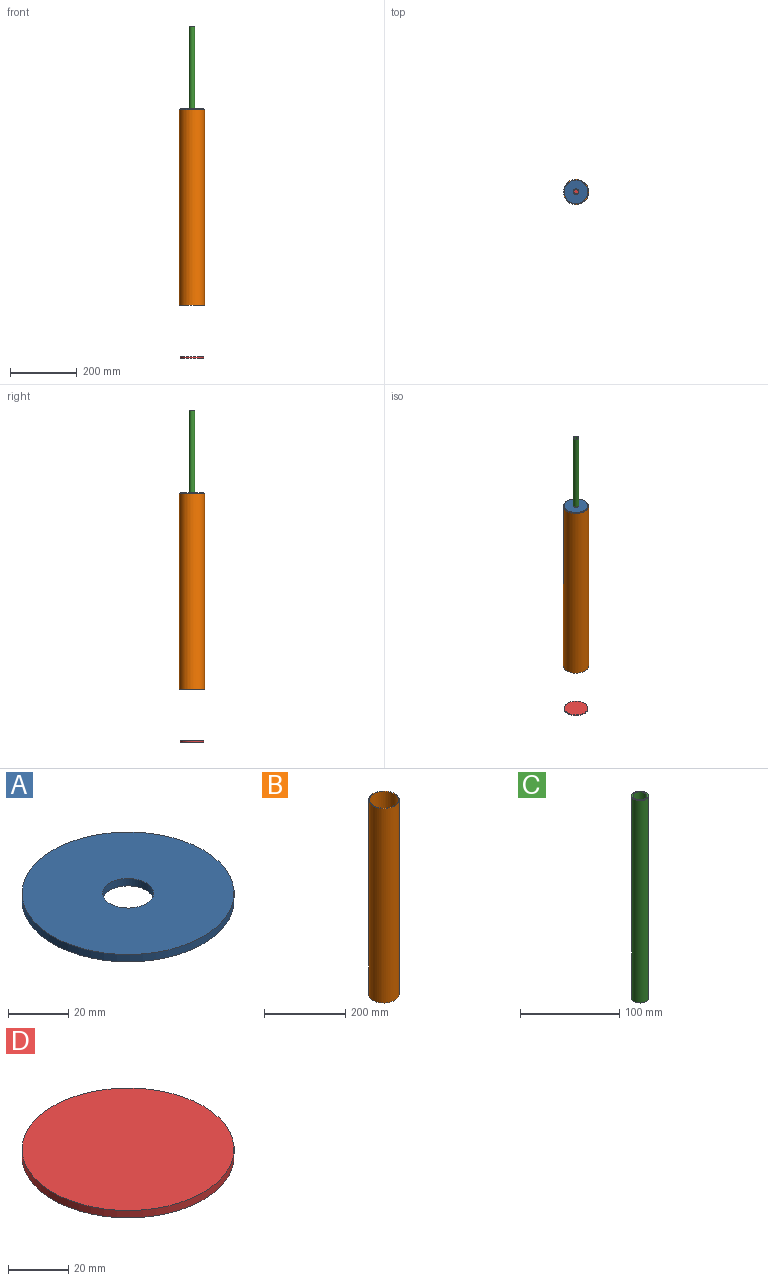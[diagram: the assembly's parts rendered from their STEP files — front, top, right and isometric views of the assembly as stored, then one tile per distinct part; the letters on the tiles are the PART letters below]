
ASSEMBLY  parts=4 mates=3
PART A: 4 faces, bbox 70.5x70.5x3 mm
  f0: cylinder r=35.25mm len=70.5mm, axis (0,0,-1), area 664.4mm2, adj f1,f2
  f1: plane 70.5x70.5mm, normal (0,0,1), area 3676.6mm2, adj f0,f3
  f2: plane 70.5x70.5mm, normal (0,0,-1), area 3676.6mm2, adj f0,f3
  f3: cylinder r=8.5mm len=17mm, axis (0,0,1), area 160.2mm2, adj f1,f2
PART B: 4 faces, bbox 75x75x585 mm
  f0: cylinder r=35.5mm len=585mm, axis (0,0,-1), area 130486.1mm2, adj f2,f3
  f1: cylinder r=37.5mm len=585mm, axis (0,0,-1), area 137837.4mm2, adj f2,f3
  f2: plane 75x75mm, normal (0,0,1), area 458.7mm2, adj f0,f1
  f3: plane 75x75mm, normal (0,0,-1), area 458.7mm2, adj f0,f1
PART C: 4 faces, bbox 17x17x250 mm
  f0: cylinder r=7mm len=250mm, axis (0,0,-1), area 10995.6mm2, adj f2,f3
  f1: cylinder r=8.5mm len=250mm, axis (0,0,-1), area 13351.8mm2, adj f2,f3
  f2: plane 17x17mm, normal (0,0,1), area 73mm2, adj f0,f1
  f3: plane 17x17mm, normal (0,0,-1), area 73mm2, adj f0,f1
PART D: 3 faces, bbox 70.5x70.5x3 mm
  f0: cylinder r=35.25mm len=70.5mm, axis (0,0,-1), area 664.4mm2, adj f1,f2
  f1: plane 70.5x70.5mm, normal (0,0,1), area 3903.6mm2, adj f0
  f2: plane 70.5x70.5mm, normal (0,0,-1), area 3903.6mm2, adj f0
PLACE A rot(axis=(0,0,-1),86.4deg) t=(-6.91,135.86,571.79)mm
PLACE B t=(-6.91,135.86,-14.21)mm
PLACE C rot(axis=(0,0,1),56.7deg) t=(-6.91,135.86,571.29)mm
PLACE D rot(axis=(0,0,1),112.6deg) t=(-6.91,135.86,-170.18)mm
MATE cylindrical B.f1 <-> D.f0  axis (0,0,-1) through (-6.91,135.86,278.29)mm
MATE cylindrical B.f1 <-> A.f0  axis (0,0,-1) through (-6.91,135.86,278.29)mm
MATE cylindrical C.f1 <-> B.f1  axis (0,0,-1) through (-6.91,135.86,696.29)mm
